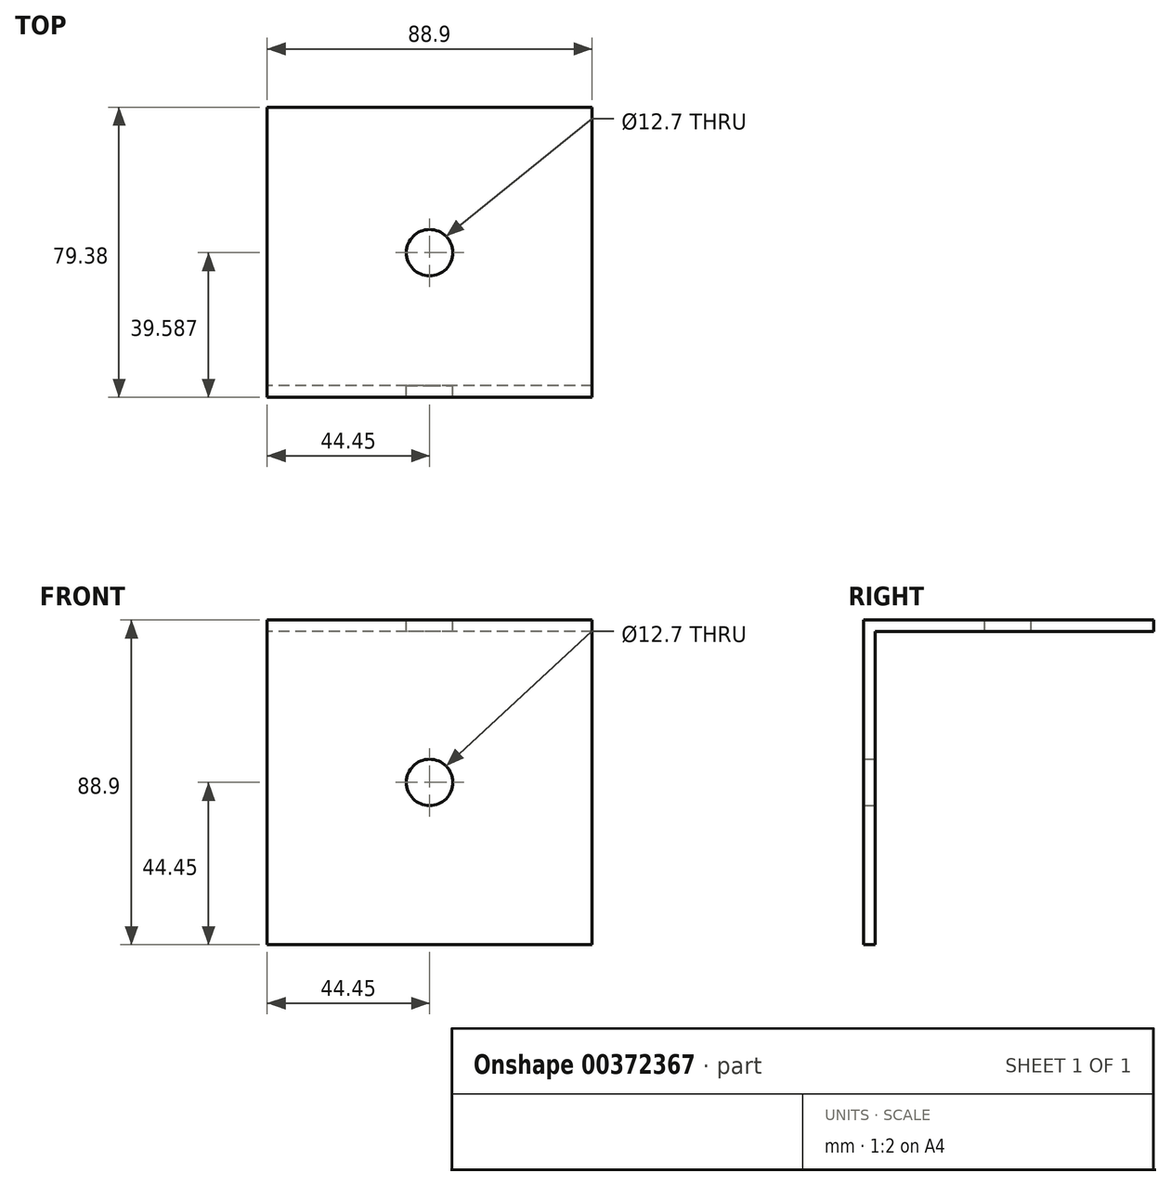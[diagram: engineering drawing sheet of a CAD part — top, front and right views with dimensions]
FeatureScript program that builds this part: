
annotation { "Feature Type Name" : "Feature", "Feature Type Description" : "" }
export const myFeature = defineFeature(function(context is Context, id is Id, definition is map)
    precondition{}
    {
        {
            var Q0;
            Q0=qCreatedBy(makeId("Front.planeOp"),FACE);
            var sketch = newSketch(context, id + "F0", { "sketchPlane" : qUnion([Q0])});
            skLineSegment(sketch, "E0.bottom", {"start": v(-44.45, 44.45) * mm, "end": v(44.45, 44.45) * mm});
            skLineSegment(sketch, "E0.top", {"start": v(-44.45, -44.45) * mm, "end": v(44.45, -44.45) * mm});
            skLineSegment(sketch, "E0.left", {"start": v(-44.45, 44.45) * mm, "end": v(-44.45, -44.45) * mm});
            skLineSegment(sketch, "E0.right", {"start": v(44.45, 44.45) * mm, "end": v(44.45, -44.45) * mm});
            skPoint(sketch, "E0.middle", {"position": v(0, 0) * mm});
            skSolve(sketch);
        }
        {
            var Q0;
            Q0 = qSketchRegion(id + "F0", true);
            extrude(context, id + "F1", {"entities" : qUnion([Q0]), "depth" : 3.17 * mm});
        }
        {
            var Q0;
            Q0=makeQuery(id+"F1.opExtrude","CAP_FACE",FACE,{"disambiguationData":[OSD([sQuery(id+"F0.wireOp",EDGE,"E0.bottom"),sQuery(id+"F0.wireOp",EDGE,"E0.top"),sQuery(id+"F0.wireOp",EDGE,"E0.left"),sQuery(id+"F0.wireOp",EDGE,"E0.right")])],"isStart":true});
            var sketch = newSketch(context, id + "F2", { "sketchPlane" : qUnion([Q0])});
            skLineSegment(sketch, "E1.bottom", {"start": v(-44.45, 44.45) * mm, "end": v(44.45, 44.45) * mm});
            skLineSegment(sketch, "E1.top", {"start": v(-44.45, 41.28) * mm, "end": v(44.45, 41.28) * mm});
            skLineSegment(sketch, "E1.left", {"start": v(-44.45, 44.45) * mm, "end": v(-44.45, 41.28) * mm});
            skLineSegment(sketch, "E1.right", {"start": v(44.45, 44.45) * mm, "end": v(44.45, 41.28) * mm});
            skSolve(sketch);
        }
        {
            var Q0;
            Q0 = qSketchRegion(id + "F2", true);
            extrude(context, id + "F3", {"entities" : qUnion([Q0]), "operationType" : NewBodyOperationType.ADD, "depth" : 76.2 * mm});
        }
        {
            var Q0;
            Q0=makeQuery(id+"F1.opExtrude","CAP_FACE",FACE,{"disambiguationData":[OSD([sQuery(id+"F0.wireOp",EDGE,"E0.bottom"),sQuery(id+"F0.wireOp",EDGE,"E0.top"),sQuery(id+"F0.wireOp",EDGE,"E0.left"),sQuery(id+"F0.wireOp",EDGE,"E0.right")])],"isStart":true});
            var sketch = newSketch(context, id + "F4", { "sketchPlane" : qUnion([Q0])});
            skCircle(sketch, "E2", {"center": v(0, 0) * mm, "radius": 6.35 * mm});
            skSolve(sketch);
        }
        {
            var Q0;
            Q0=makeQuery(id+"F4.imprint","IMPRINT",FACE,{"disambiguationData":[TD([[makeQuery(id+"F4.imprint","IMPRINT",EDGE,{"derivedFrom":sQuery(id+"F4.wireOp",EDGE,"E2")}),1.0]])]});
            var Q1;
            Q1=sQuery(id+"F4.wireOp",EDGE,"E2");
            extrude(context, id + "F5", {"entities" : qUnion([Q0]), "operationType" : NewBodyOperationType.REMOVE, "surfaceEntities" : qUnion([Q1]), "oppositeDirection" : true, "depth" : 3.17 * mm});
        }
        {
            var Q0;
            Q0=makeQuery(id+"F3.boolean.opBoolean","MERGE",FACE,{"derivedFrom":[makeQuery(id+"F1.opExtrude","SWEPT_FACE",FACE,{"disambiguationData":[OSD([sQuery(id+"F0.wireOp",EDGE,"E0.bottom")])]}),makeQuery(id+"F3.opExtrude","SWEPT_FACE",FACE,{"disambiguationData":[OSD([sQuery(id+"F2.wireOp",EDGE,"E1.bottom")])]})]});
            var sketch = newSketch(context, id + "F6", { "sketchPlane" : qUnion([Q0])});
            skPoint(sketch, "E3.middle", {"position": v(0, 36.4) * mm});
            skCircle(sketch, "E4", {"center": v(0, 36.4) * mm, "radius": 6.35 * mm});
            skSolve(sketch);
        }
        {
            var Q0;
            Q0=makeQuery(id+"F6.imprint","IMPRINT",FACE,{"disambiguationData":[TD([[makeQuery(id+"F6.imprint","IMPRINT",EDGE,{"derivedFrom":sQuery(id+"F6.wireOp",EDGE,"E4")}),1.0]])]});
            var Q1;
            Q1=sQuery(id+"F6.wireOp",EDGE,"E4");
            extrude(context, id + "F7", {"entities" : qUnion([Q0]), "operationType" : NewBodyOperationType.REMOVE, "surfaceEntities" : qUnion([Q1]), "oppositeDirection" : true, "depth" : 3.17 * mm});
        }
    });
